# Revit family: Safety-Equipment_Formed-Metal-Guards_Omega-Industrial_Heavy-Duty-Pipe-Downspout-Guard_Wall-Mount
name_source: partatom
category: Generic Models
units: mm (PartAtom-declared; Revit-internal decimal feet)

## family parameters
Always vertical = Yes
Can host rebar = No
Classification Number = 23.30.80.17
Cut with Voids When Loaded = No
Maintain Annotation Orientation = No
Part Type = Normal
Room Calculation Point = No
Round Connector Dimension = Use Diameter
Shared = No
Work Plane-Based = Yes

## types (2) — shared parameters
Assembly Code = E1090
Default Elevation = 4' - 0"
Description = Pipe and Downspout Guard
Expected Lifespan (Years) = 25
Guard Material = Omega_1/2 in Steel
Installation Phase = Industrial Safety Equipment
Keynote = 05 58 23
Manufacturer = Omega Industrial Products, Inc.
Manufacturer Fax = 262-284-4199
Manufacturer Website = https://www.omegaindl.com
Model = OM3391-WM
Product Data = https://www.arcat.com
Product Properties = https://www.omegaindl.com
Revision = R0_06-2018
Sales Information = https://www.omegaindl.com
Send Message = https://www.omegaindl.com
Specification = https://www.arcat.com
URL = https://www.arcat.com
Unit Height = 3' - 0"
zero-valued in all types: Maintenance Schedule (Months), Warranty Duration (Years)

## per-type parameters (varying)
| type | Guard Outside Radius | Unit Width |
| 10in x 36in | 0' - 10 3/4" | 1' - 2 3/4" |
| 12in x 36in | 1' - 0 3/4" | 1' - 4 3/4" |

## geometry (parser evidence)
native form markers: Blend x42, Sweep x2
no freeform markers — native parametric forms only
